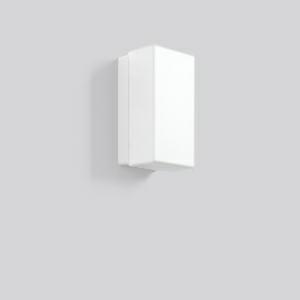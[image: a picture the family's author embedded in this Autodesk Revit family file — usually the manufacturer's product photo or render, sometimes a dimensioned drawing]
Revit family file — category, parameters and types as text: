
# Revit family: rechteck_21146_002_7167
name_source: partatom
category: Lighting Fixtures
units: mm (PartAtom-declared; Revit-internal decimal feet)

## family parameters
Cut with Voids When Loaded = No
Host = Face
Light Source = No
Part Type = Normal
Room Calculation Point = No
Round Connector Dimension = Use Diameter
Shared = No

## types (1)
- RECHTECK (1 x QA60/clear E27, 700 lm, 46 W, 3000)
    Apparent Load = 46 VA
    CIE Flux Codes = 35 64 86 74 50
    Color Rendering = 90
    Color Temperature = 3000
    Default Elevation = 1800 mm
    Description = Series: RECHTECK
Rectangular surface-mounted luminaire in classic design. Base: plastic. Opal glass: mouth-blown, satin finish. Diffuser fastening: spring system. Suitable for Ceiling mounting, Wall (surface). IP 43 ceiling mounting, IP 44 wall mounting. 
Colour: white
Length: 220 mm
Width: 120 mm
Height: 105 mm
Lamp: A60
Number of lamps: 1
Wattage: 60 W
Socket: E27
System power: 46 W
Rated luminous flux: 350 lm
Luminous efficiency: 8 lm/W
Control gear: Converter not necessary
Protection class: II
Type of protection: IP 43
    Height = 105 mm
    Lamp = 1 x QA60/clear E27
    Lamp Light Flux = 700 lm
    Lamp Power = 46 W
    Lamp count = 1
    Length = 220 mm
    Lifetime = 3000 h
    Luminous efficacy = 8 lm/W
    Manufacturer = RZB
    ModVariant = No
    Model = 21146.002
    Mounting Place = Ceiling, Wall
    Mounting Type = Surface mounted
    Number of Poles = 1
    OnlyDefault = Yes
    Power Factor = 1
    Product Name = RECHTECK
    Product group = Surface mounted ceiling and wall luminaires
    ProductGroupID = 305
    Protection Class = Protection class II
    Protection Degree = IP 43
    RLX_Detail_Level = 1
    RLX_Emergency_Light_Flux = 0 lm
    RLX_Emergency_Type = 0
    RLX_Emergency_Type_DB = No
    RlxData = <blob elided: 19409 chars, md5=840e0787>
    Socket = E27
    Standby Power = 0 W
    System Light Flux = 352 lm
    System Power = 46 W
    Type Comments = Product without accessories
    Type Image = 21146.002.jpg
    URL = http://relux.com
    VarID = ---
    Voltage = 230 V
    Voltage Range = 220-240 V
    Weight = 0.00 kg
    Width = 120 mm

## geometry (parser evidence)
native form markers: Blend x4, Sweep x15
no freeform markers — native parametric forms only
